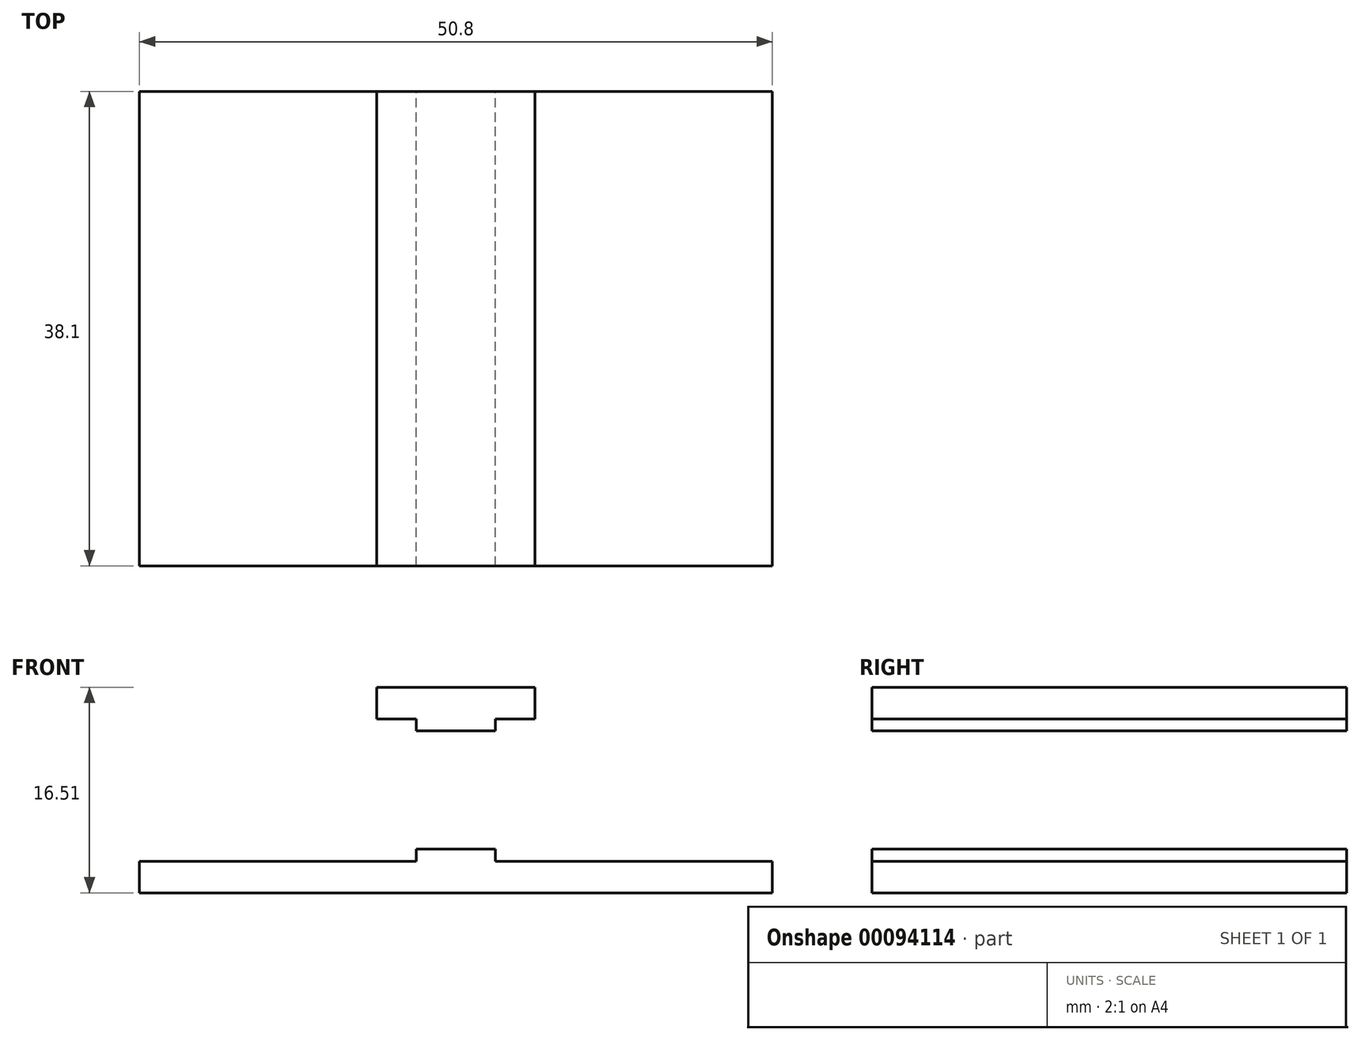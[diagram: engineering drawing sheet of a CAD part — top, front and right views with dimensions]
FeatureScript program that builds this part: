
annotation { "Feature Type Name" : "Feature", "Feature Type Description" : "" }
export const myFeature = defineFeature(function(context is Context, id is Id, definition is map)
    precondition{}
    {
        {
            var Q0;
            Q0=qCreatedBy(makeId("Front.planeOp"),FACE);
            var sketch = newSketch(context, id + "F0", { "sketchPlane" : qUnion([Q0])});
            skLineSegment(sketch, "E0.bottom", {"start": v(0, 0) * mm, "end": v(12.7, 0) * mm});
            skLineSegment(sketch, "E0.top", {"start": v(0, -2.54) * mm, "end": v(12.7, -2.54) * mm});
            skLineSegment(sketch, "E0.left", {"start": v(0, 0) * mm, "end": v(0, -2.54) * mm});
            skLineSegment(sketch, "E0.right", {"start": v(12.7, 0) * mm, "end": v(12.7, -2.54) * mm});
            skCircle(sketch, "E1", {"center": v(6.35, -8.26) * mm, "radius": 5.72 * mm});
            skCircle(sketch, "E2", {"center": v(6.35, -8.26) * mm, "radius": 3.18 * mm});
            skLineSegment(sketch, "E3.bottom", {"start": v(-19.05, -13.97) * mm, "end": v(31.75, -13.97) * mm});
            skLineSegment(sketch, "E3.top", {"start": v(-19.05, -16.51) * mm, "end": v(31.75, -16.51) * mm});
            skLineSegment(sketch, "E3.left", {"start": v(-19.05, -13.97) * mm, "end": v(-19.05, -16.51) * mm});
            skLineSegment(sketch, "E3.right", {"start": v(31.75, -13.97) * mm, "end": v(31.75, -16.5) * mm});
            skLineSegment(sketch, "E4", {"start": v(6.35, 11.52) * mm, "end": v(6.35, -36.14) * mm, "construction": true});
            skPoint(sketch, "E5", {"position": v(6.35, -2.54) * mm});
            skPoint(sketch, "E6", {"position": v(6.35, -13.97) * mm});
            skLineSegment(sketch, "E7", {"start": v(9.26, -6.99) * mm, "end": v(11.92, -6.99) * mm});
            skLineSegment(sketch, "E8", {"start": v(9.26, -9.53) * mm, "end": v(11.92, -9.53) * mm});
            skLineSegment(sketch, "E9.bottom", {"start": v(3.18, -2.54) * mm, "end": v(9.53, -2.54) * mm});
            skLineSegment(sketch, "E9.top", {"start": v(3.18, -3.5) * mm, "end": v(9.53, -3.5) * mm});
            skLineSegment(sketch, "E9.left", {"start": v(3.18, -2.54) * mm, "end": v(3.18, -3.5) * mm});
            skLineSegment(sketch, "E9.right", {"start": v(9.53, -2.54) * mm, "end": v(9.53, -3.5) * mm});
            skLineSegment(sketch, "E10.bottom", {"start": v(3.18, -13) * mm, "end": v(9.53, -13) * mm});
            skLineSegment(sketch, "E10.top", {"start": v(3.18, -13.97) * mm, "end": v(9.53, -13.97) * mm});
            skLineSegment(sketch, "E10.left", {"start": v(3.18, -13) * mm, "end": v(3.18, -13.97) * mm});
            skLineSegment(sketch, "E10.right", {"start": v(9.53, -13) * mm, "end": v(9.53, -13.97) * mm});
            skSolve(sketch);
        }
        {
            var Q0;
            Q0=makeQuery(id+"F0.imprint","IMPRINT",FACE,{"disambiguationData":[TD([[makeQuery(id+"F0.imprint","IMPRINT",EDGE,{"derivedFrom":sQuery(id+"F0.wireOp",EDGE,"E0.bottom")}),-1.0]])]});
            var Q1;
            {var subQ0=sQuery(id+"F0.wireOp",EDGE,"E9.left");Q1=makeQuery(id+"F0.imprint","IMPRINT",FACE,{"disambiguationData":[TD([[makeQuery(id+"F0.imprint","IMPRINT",EDGE,{"derivedFrom":subQ0}),1.0]])]});}
            var Q2;
            {var subQ0=sQuery(id+"F0.wireOp",EDGE,"E9.top");Q2=makeQuery(id+"F0.imprint","IMPRINT",FACE,{"disambiguationData":[TD([[makeQuery(id+"F0.imprint","IMPRINT",EDGE,{"derivedFrom":subQ0}),1.0]])]});}
            var Q3;
            {var subQ0=sQuery(id+"F0.wireOp",EDGE,"E9.right");Q3=makeQuery(id+"F0.imprint","IMPRINT",FACE,{"disambiguationData":[TD([[makeQuery(id+"F0.imprint","IMPRINT",EDGE,{"derivedFrom":subQ0}),-1.0]])]});}
            var Q4;
            {var subQ0=sQuery(id+"F0.wireOp",EDGE,"E7");Q4=makeQuery(id+"F0.imprint","IMPRINT",FACE,{"disambiguationData":[TD([[makeQuery(id+"F0.imprint","IMPRINT",EDGE,{"derivedFrom":subQ0}),1.0]])]});}
            var Q5;
            {var subQ0=sQuery(id+"F0.wireOp",EDGE,"E10.bottom");Q5=makeQuery(id+"F0.imprint","IMPRINT",FACE,{"disambiguationData":[TD([[makeQuery(id+"F0.imprint","IMPRINT",EDGE,{"derivedFrom":subQ0}),-1.0]])]});}
            var Q6;
            {var subQ0=sQuery(id+"F0.wireOp",EDGE,"E10.right");Q6=makeQuery(id+"F0.imprint","IMPRINT",FACE,{"disambiguationData":[TD([[makeQuery(id+"F0.imprint","IMPRINT",EDGE,{"derivedFrom":subQ0}),-1.0]])]});}
            var Q7;
            {var subQ0=sQuery(id+"F0.wireOp",EDGE,"E10.left");Q7=makeQuery(id+"F0.imprint","IMPRINT",FACE,{"disambiguationData":[TD([[makeQuery(id+"F0.imprint","IMPRINT",EDGE,{"derivedFrom":subQ0}),1.0]])]});}
            var Q8;
            Q8=makeQuery(id+"F0.imprint","IMPRINT",FACE,{"disambiguationData":[TD([[makeQuery(id+"F0.imprint","IMPRINT",EDGE,{"derivedFrom":sQuery(id+"F0.wireOp",EDGE,"E3.top")}),1.0]])]});
            extrude(context, id + "F1", {"entities" : qUnion([Q0, Q1, Q2, Q3, Q4, Q5, Q6, Q7, Q8]), "depth" : 38.1 * mm});
        }
    });
